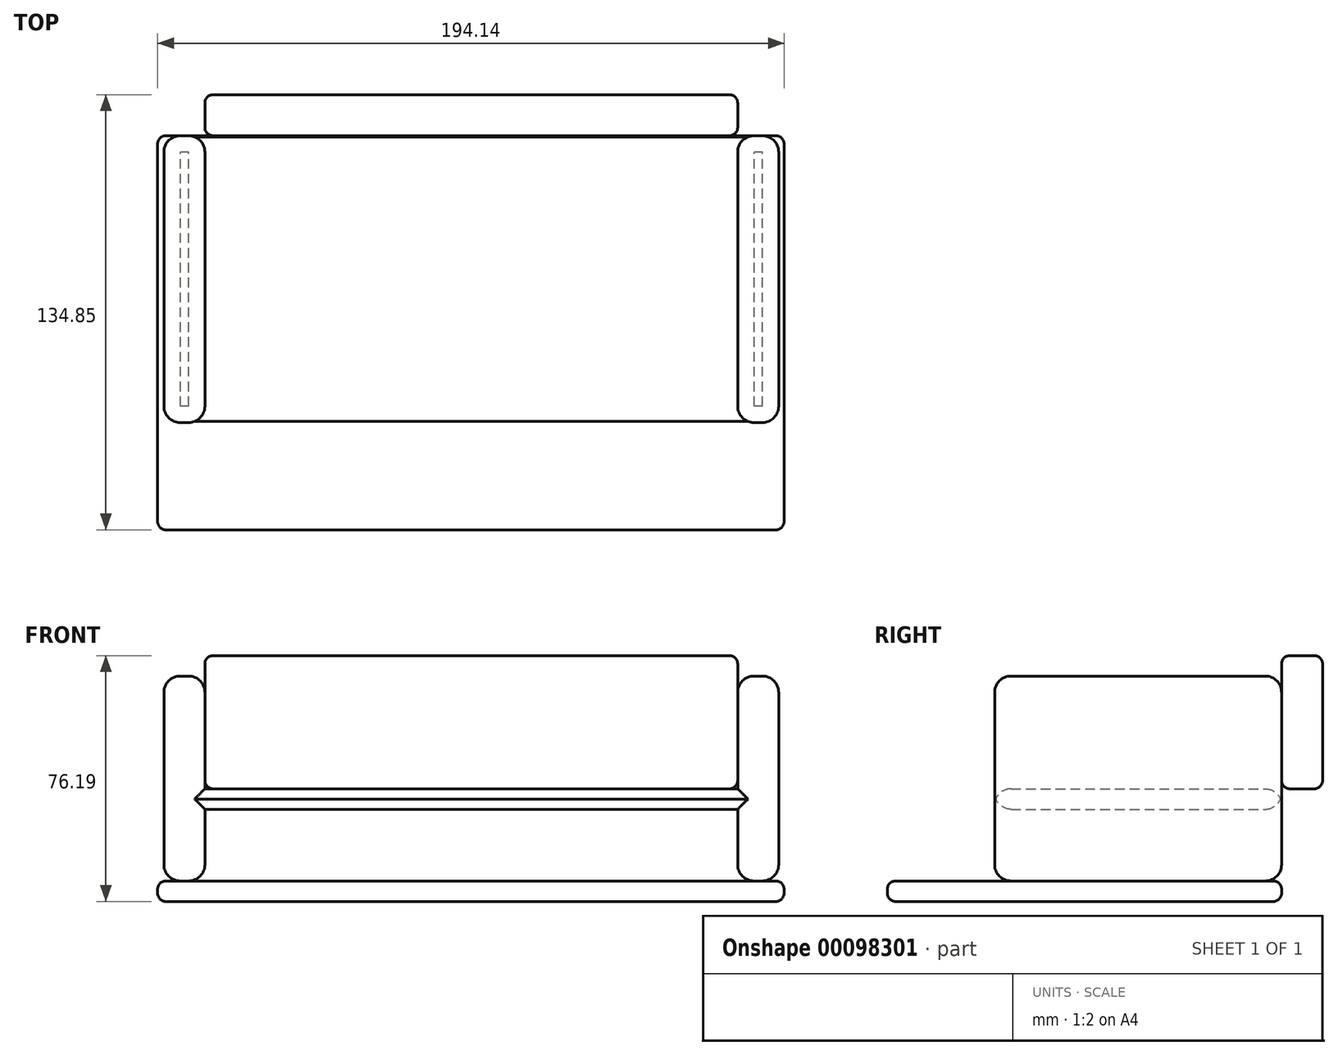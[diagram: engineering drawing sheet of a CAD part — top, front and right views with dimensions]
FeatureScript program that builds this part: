
annotation { "Feature Type Name" : "Feature", "Feature Type Description" : "" }
export const myFeature = defineFeature(function(context is Context, id is Id, definition is map)
    precondition{}
    {
        {
            var Q0;
            Q0=qCreatedBy(makeId("Front.planeOp"),FACE);
            var sketch = newSketch(context, id + "F0", { "sketchPlane" : qUnion([Q0])});
            skLineSegment(sketch, "E0.bottom", {"start": v(88.9, -34.92) * mm, "end": v(-88.9, -34.93) * mm});
            skLineSegment(sketch, "E0.top", {"start": v(88.9, 34.93) * mm, "end": v(82.55, 34.93) * mm});
            skLineSegment(sketch, "E0.left", {"start": v(88.9, -34.92) * mm, "end": v(88.9, 34.93) * mm});
            skLineSegment(sketch, "E0.right", {"start": v(-88.9, -34.93) * mm, "end": v(-88.9, 34.92) * mm});
            skPoint(sketch, "E0.middle", {"position": v(0, 0) * mm});
            skLineSegment(sketch, "E1.1", {"start": v(82.55, -28.57) * mm, "end": v(82.55, -6.35) * mm});
            skLineSegment(sketch, "E1.2", {"start": v(88.9, -28.57) * mm, "end": v(-88.9, -28.58) * mm});
            skLineSegment(sketch, "E1.3", {"start": v(-82.55, -28.58) * mm, "end": v(-82.55, -6.35) * mm});
            skLineSegment(sketch, "E2.trimOffspring", {"start": v(-82.55, 34.92) * mm, "end": v(-88.9, 34.92) * mm});
            skLineSegment(sketch, "E3", {"start": v(-82.55, 0) * mm, "end": v(82.55, 0) * mm});
            skLineSegment(sketch, "E4.0", {"start": v(-82.55, -6.35) * mm, "end": v(82.55, -6.35) * mm});
            skLineSegment(sketch, "E5.trimOffspring", {"start": v(-82.55, 0) * mm, "end": v(-82.55, 34.92) * mm});
            skLineSegment(sketch, "E6.trimOffspring", {"start": v(82.55, 0) * mm, "end": v(82.55, 34.93) * mm});
            skLineSegment(sketch, "E7", {"start": v(-82.55, 34.92) * mm, "end": v(-82.55, 41.27) * mm});
            skLineSegment(sketch, "E8", {"start": v(-82.55, 41.27) * mm, "end": v(82.55, 41.27) * mm});
            skLineSegment(sketch, "E9", {"start": v(82.55, 41.27) * mm, "end": v(82.55, 34.93) * mm});
            skSolve(sketch);
        }
        {
            var Q0;
            {var subQ8=sQuery(id+"F0.wireOp",EDGE,"E0.top");Q0=makeQuery(id+"F0.imprint","IMPRINT",FACE,{"disambiguationData":[TD([[makeQuery(id+"F0.imprint","IMPRINT",EDGE,{"derivedFrom":subQ8}),1.0]])]});}
            extrude(context, id + "F1", {"entities" : qUnion([Q0]), "depth" : 88.9 * mm});
        }
        {
            var Q0;
            Q0=makeQuery(id+"F1.opExtrude","SWEPT_FACE",FACE,{"disambiguationData":[OSD([sQuery(id+"F0.wireOp",EDGE,"E0.right")])]});
            extrude(context, id + "F2", {"entities" : qUnion([Q0]), "operationType" : NewBodyOperationType.ADD, "depth" : 6.35 * mm});
        }
        {
            var Q0;
            Q0=makeQuery(id+"F1.opExtrude","SWEPT_FACE",FACE,{"disambiguationData":[OSD([sQuery(id+"F0.wireOp",EDGE,"E0.left")])]});
            extrude(context, id + "F3", {"entities" : qUnion([Q0]), "operationType" : NewBodyOperationType.ADD, "depth" : 6.35 * mm});
        }
        {
            var Q0;
            {var subQ0=sQuery(id+"F0.wireOp",EDGE,"E0.left");var subQ1=sQuery(id+"F0.wireOp",EDGE,"E0.right");Q0=makeQuery(id+"F3.boolean.opBoolean","MERGE",FACE,{"derivedFrom":[makeQuery(id+"F2.boolean.opBoolean","MERGE",FACE,{"derivedFrom":[makeQuery(id+"F1.opExtrude","CAP_FACE",FACE,{"disambiguationData":[OSD([sQuery(id+"F0.wireOp",EDGE,"E0.top"),subQ0,subQ1,sQuery(id+"F0.wireOp",EDGE,"E1.1"),sQuery(id+"F0.wireOp",EDGE,"E1.2"),sQuery(id+"F0.wireOp",EDGE,"E1.3"),sQuery(id+"F0.wireOp",EDGE,"E2.trimOffspring"),sQuery(id+"F0.wireOp",EDGE,"E3"),sQuery(id+"F0.wireOp",EDGE,"E4.0"),sQuery(id+"F0.wireOp",EDGE,"E5.trimOffspring"),sQuery(id+"F0.wireOp",EDGE,"E6.trimOffspring")])],"isStart":false}),makeQuery(id+"F2.opExtrude","SWEPT_FACE",FACE,{"disambiguationData":[OSD([subQ1]),TDD([makeQuery(id+"F1.opExtrude","CAP_EDGE",EDGE,{"disambiguationData":[OSD([subQ1])],"isStart":false})])]})]}),makeQuery(id+"F3.opExtrude","SWEPT_FACE",FACE,{"disambiguationData":[OSD([subQ0]),TDD([makeQuery(id+"F1.opExtrude","CAP_EDGE",EDGE,{"disambiguationData":[OSD([subQ0])],"isStart":false})])]})]});}
            var Q1;
            {var subQ0=sQuery(id+"F0.wireOp",EDGE,"E2.trimOffspring");Q1=makeQuery(id+"F2.boolean.opBoolean","MERGE",FACE,{"derivedFrom":[makeQuery(id+"F1.opExtrude","SWEPT_FACE",FACE,{"disambiguationData":[OSD([subQ0])]}),makeQuery(id+"F2.opExtrude","SWEPT_FACE",FACE,{"disambiguationData":[OSD([sQuery(id+"F0.wireOp",EDGE,"E0.right"),subQ0])]})]});}
            var Q2;
            {var subQ0=sQuery(id+"F0.wireOp",EDGE,"E0.top");Q2=makeQuery(id+"F3.boolean.opBoolean","MERGE",FACE,{"derivedFrom":[makeQuery(id+"F1.opExtrude","SWEPT_FACE",FACE,{"disambiguationData":[OSD([subQ0])]}),makeQuery(id+"F3.opExtrude","SWEPT_FACE",FACE,{"disambiguationData":[OSD([subQ0,sQuery(id+"F0.wireOp",EDGE,"E0.left")])]})]});}
            var Q3;
            {var subQ0=sQuery(id+"F0.wireOp",EDGE,"E1.2");var subQ1=sQuery(id+"F0.wireOp",EDGE,"E0.left");Q3=makeQuery(id+"F3.boolean.opBoolean","MERGE",FACE,{"derivedFrom":[makeQuery(id+"F1.opExtrude","SWEPT_FACE",FACE,{"disambiguationData":[OSD([subQ0]),TDD([makeQuery(id+"F0.imprint","IMPRINT",EDGE,{"disambiguationData":[TD([[makeQuery(id+"F0.imprint","INTERSECT",VERTEX,{"derivedFrom":[sQuery(id+"F0.wireOp",EDGE,"E1.1"),subQ0]}),1.0]])],"derivedFrom":subQ0})])]}),makeQuery(id+"F3.opExtrude","SWEPT_FACE",FACE,{"disambiguationData":[OSD([subQ1,subQ0])]})]});}
            var Q4;
            {var subQ0=sQuery(id+"F0.wireOp",EDGE,"E1.2");var subQ1=sQuery(id+"F0.wireOp",EDGE,"E0.right");Q4=makeQuery(id+"F2.boolean.opBoolean","MERGE",FACE,{"derivedFrom":[makeQuery(id+"F1.opExtrude","SWEPT_FACE",FACE,{"disambiguationData":[OSD([subQ0]),TDD([makeQuery(id+"F0.imprint","IMPRINT",EDGE,{"disambiguationData":[TD([[makeQuery(id+"F0.imprint","INTERSECT",VERTEX,{"derivedFrom":[subQ1,subQ0]}),1.0]])],"derivedFrom":subQ0})])]}),makeQuery(id+"F2.opExtrude","SWEPT_FACE",FACE,{"disambiguationData":[OSD([subQ1,subQ0])]})]});}
            var Q5;
            {var subQ0=sQuery(id+"F0.wireOp",EDGE,"E0.left");var subQ1=sQuery(id+"F0.wireOp",EDGE,"E0.right");Q5=makeQuery(id+"F3.boolean.opBoolean","MERGE",FACE,{"derivedFrom":[makeQuery(id+"F2.boolean.opBoolean","MERGE",FACE,{"derivedFrom":[makeQuery(id+"F1.opExtrude","CAP_FACE",FACE,{"disambiguationData":[OSD([sQuery(id+"F0.wireOp",EDGE,"E0.top"),subQ0,subQ1,sQuery(id+"F0.wireOp",EDGE,"E1.1"),sQuery(id+"F0.wireOp",EDGE,"E1.2"),sQuery(id+"F0.wireOp",EDGE,"E1.3"),sQuery(id+"F0.wireOp",EDGE,"E2.trimOffspring"),sQuery(id+"F0.wireOp",EDGE,"E3"),sQuery(id+"F0.wireOp",EDGE,"E4.0"),sQuery(id+"F0.wireOp",EDGE,"E5.trimOffspring"),sQuery(id+"F0.wireOp",EDGE,"E6.trimOffspring")])],"isStart":true}),makeQuery(id+"F2.opExtrude","SWEPT_FACE",FACE,{"disambiguationData":[OSD([subQ1]),TDD([makeQuery(id+"F1.opExtrude","CAP_EDGE",EDGE,{"disambiguationData":[OSD([subQ1])],"isStart":true})])]})]}),makeQuery(id+"F3.opExtrude","SWEPT_FACE",FACE,{"disambiguationData":[OSD([subQ0]),TDD([makeQuery(id+"F1.opExtrude","CAP_EDGE",EDGE,{"disambiguationData":[OSD([subQ0])],"isStart":true})])]})]});}
            fillet(context, id + "F4", {"entities" : qUnion([Q0, Q1, Q2, Q3, Q4, Q5]), "radius" : 5.08 * mm, "tangentPropagation" : true, "allowEdgeOverflow" : false});
        }
        {
            var Q0;
            {var subQ5=sQuery(id+"F0.wireOp",EDGE,"E0.bottom");Q0=makeQuery(id+"F0.imprint","IMPRINT",FACE,{"disambiguationData":[TD([[makeQuery(id+"F0.imprint","IMPRINT",EDGE,{"derivedFrom":subQ5}),-1.0]])]});}
            extrude(context, id + "F5", {"entities" : qUnion([Q0]), "operationType" : NewBodyOperationType.ADD, "depth" : 122.15 * mm});
        }
        {
            var Q0;
            Q0=makeQuery(id+"F5.opExtrude","SWEPT_FACE",FACE,{"disambiguationData":[OSD([sQuery(id+"F0.wireOp",EDGE,"E0.right")])]});
            extrude(context, id + "F6", {"entities" : qUnion([Q0]), "operationType" : NewBodyOperationType.ADD, "depth" : 8.3 * mm});
        }
        {
            var Q0;
            Q0=makeQuery(id+"F5.opExtrude","SWEPT_FACE",FACE,{"disambiguationData":[OSD([sQuery(id+"F0.wireOp",EDGE,"E0.left")])]});
            extrude(context, id + "F7", {"entities" : qUnion([Q0]), "operationType" : NewBodyOperationType.ADD, "depth" : 8.04 * mm});
        }
        {
            var Q0;
            {var subQ0=sQuery(id+"F0.wireOp",EDGE,"E0.left");var subQ1=sQuery(id+"F0.wireOp",EDGE,"E0.right");Q0=makeQuery(id+"F7.boolean.opBoolean","MERGE",FACE,{"derivedFrom":[makeQuery(id+"F6.boolean.opBoolean","MERGE",FACE,{"derivedFrom":[makeQuery(id+"F5.opExtrude","CAP_FACE",FACE,{"disambiguationData":[OSD([sQuery(id+"F0.wireOp",EDGE,"E0.bottom"),subQ0,subQ1,sQuery(id+"F0.wireOp",EDGE,"E1.2")])],"isStart":false}),makeQuery(id+"F6.opExtrude","SWEPT_FACE",FACE,{"disambiguationData":[OSD([subQ1]),TDD([makeQuery(id+"F5.opExtrude","CAP_EDGE",EDGE,{"disambiguationData":[OSD([subQ1])],"isStart":false})])]})]}),makeQuery(id+"F7.opExtrude","SWEPT_FACE",FACE,{"disambiguationData":[OSD([subQ0]),TDD([makeQuery(id+"F5.opExtrude","CAP_EDGE",EDGE,{"disambiguationData":[OSD([subQ0])],"isStart":false})])]})]});}
            var Q1;
            Q1=makeQuery(id+"F7.opExtrude","CAP_FACE",FACE,{"disambiguationData":[OSD([sQuery(id+"F0.wireOp",EDGE,"E0.left")])],"isStart":false});
            var Q2;
            Q2=makeQuery(id+"F6.opExtrude","CAP_FACE",FACE,{"disambiguationData":[OSD([sQuery(id+"F0.wireOp",EDGE,"E0.right")])],"isStart":false});
            var Q3;
            {var subQ0=sQuery(id+"F0.wireOp",EDGE,"E0.left");var subQ1=sQuery(id+"F0.wireOp",EDGE,"E0.right");Q3=makeQuery(id+"F7.boolean.opBoolean","MERGE",FACE,{"derivedFrom":[makeQuery(id+"F6.boolean.opBoolean","MERGE",FACE,{"derivedFrom":[makeQuery(id+"F5.opExtrude","CAP_FACE",FACE,{"disambiguationData":[OSD([sQuery(id+"F0.wireOp",EDGE,"E0.bottom"),subQ0,subQ1,sQuery(id+"F0.wireOp",EDGE,"E1.2")])],"isStart":true}),makeQuery(id+"F6.opExtrude","SWEPT_FACE",FACE,{"disambiguationData":[OSD([subQ1]),TDD([makeQuery(id+"F5.opExtrude","CAP_EDGE",EDGE,{"disambiguationData":[OSD([subQ1])],"isStart":true})])]})]}),makeQuery(id+"F7.opExtrude","SWEPT_FACE",FACE,{"disambiguationData":[OSD([subQ0]),TDD([makeQuery(id+"F5.opExtrude","CAP_EDGE",EDGE,{"disambiguationData":[OSD([subQ0])],"isStart":true})])]})]});}
            fillet(context, id + "F8", {"entities" : qUnion([Q0, Q1, Q2, Q3]), "radius" : 2.54 * mm, "tangentPropagation" : true, "allowEdgeOverflow" : false});
        }
        {
            var Q0;
            Q0=makeQuery(id+"F0.imprint","IMPRINT",FACE,{"disambiguationData":[TD([[makeQuery(id+"F0.imprint","IMPRINT",EDGE,{"derivedFrom":sQuery(id+"F0.wireOp",EDGE,"E3")}),1.0]])]});
            extrude(context, id + "F9", {"entities" : qUnion([Q0]), "oppositeDirection" : true, "depth" : 12.7 * mm});
        }
        {
            var Q0;
            Q0=makeQuery(id+"F9.opExtrude","SWEPT_FACE",FACE,{"disambiguationData":[OSD([sQuery(id+"F0.wireOp",EDGE,"E6.trimOffspring"),sQuery(id+"F0.wireOp",EDGE,"E9")])]});
            var Q1;
            Q1=makeQuery(id+"F9.opExtrude","CAP_EDGE",EDGE,{"disambiguationData":[OSD([sQuery(id+"F0.wireOp",EDGE,"E8")])],"isStart":false});
            var Q2;
            Q2=makeQuery(id+"F9.opExtrude","CAP_EDGE",EDGE,{"disambiguationData":[OSD([sQuery(id+"F0.wireOp",EDGE,"E8")])],"isStart":true});
            var Q3;
            Q3=makeQuery(id+"F9.opExtrude","SWEPT_EDGE",EDGE,{"disambiguationData":[OSD([sQuery(id+"F0.wireOp",EDGE,"E7"),sQuery(id+"F0.wireOp",EDGE,"E8")])]});
            var Q4;
            Q4=makeQuery(id+"F9.opExtrude","CAP_EDGE",EDGE,{"disambiguationData":[OSD([sQuery(id+"F0.wireOp",EDGE,"E5.trimOffspring"),sQuery(id+"F0.wireOp",EDGE,"E7")])],"isStart":false});
            var Q5;
            Q5=makeQuery(id+"F9.opExtrude","CAP_EDGE",EDGE,{"disambiguationData":[OSD([sQuery(id+"F0.wireOp",EDGE,"E5.trimOffspring"),sQuery(id+"F0.wireOp",EDGE,"E7")])],"isStart":true});
            var Q6;
            Q6=makeQuery(id+"F9.opExtrude","CAP_EDGE",EDGE,{"disambiguationData":[OSD([sQuery(id+"F0.wireOp",EDGE,"E3")])],"isStart":false});
            var Q7;
            Q7=makeQuery(id+"F9.opExtrude","CAP_EDGE",EDGE,{"disambiguationData":[OSD([sQuery(id+"F0.wireOp",EDGE,"E3")])],"isStart":true});
            var Q8;
            Q8=makeQuery(id+"F9.opExtrude","SWEPT_EDGE",EDGE,{"disambiguationData":[OSD([sQuery(id+"F0.wireOp",EDGE,"E3"),sQuery(id+"F0.wireOp",EDGE,"E5.trimOffspring")])]});
            fillet(context, id + "F10", {"entities" : qUnion([Q0, Q1, Q2, Q3, Q4, Q5, Q6, Q7, Q8]), "radius" : 2.54 * mm, "tangentPropagation" : true, "allowEdgeOverflow" : false});
        }
    });
